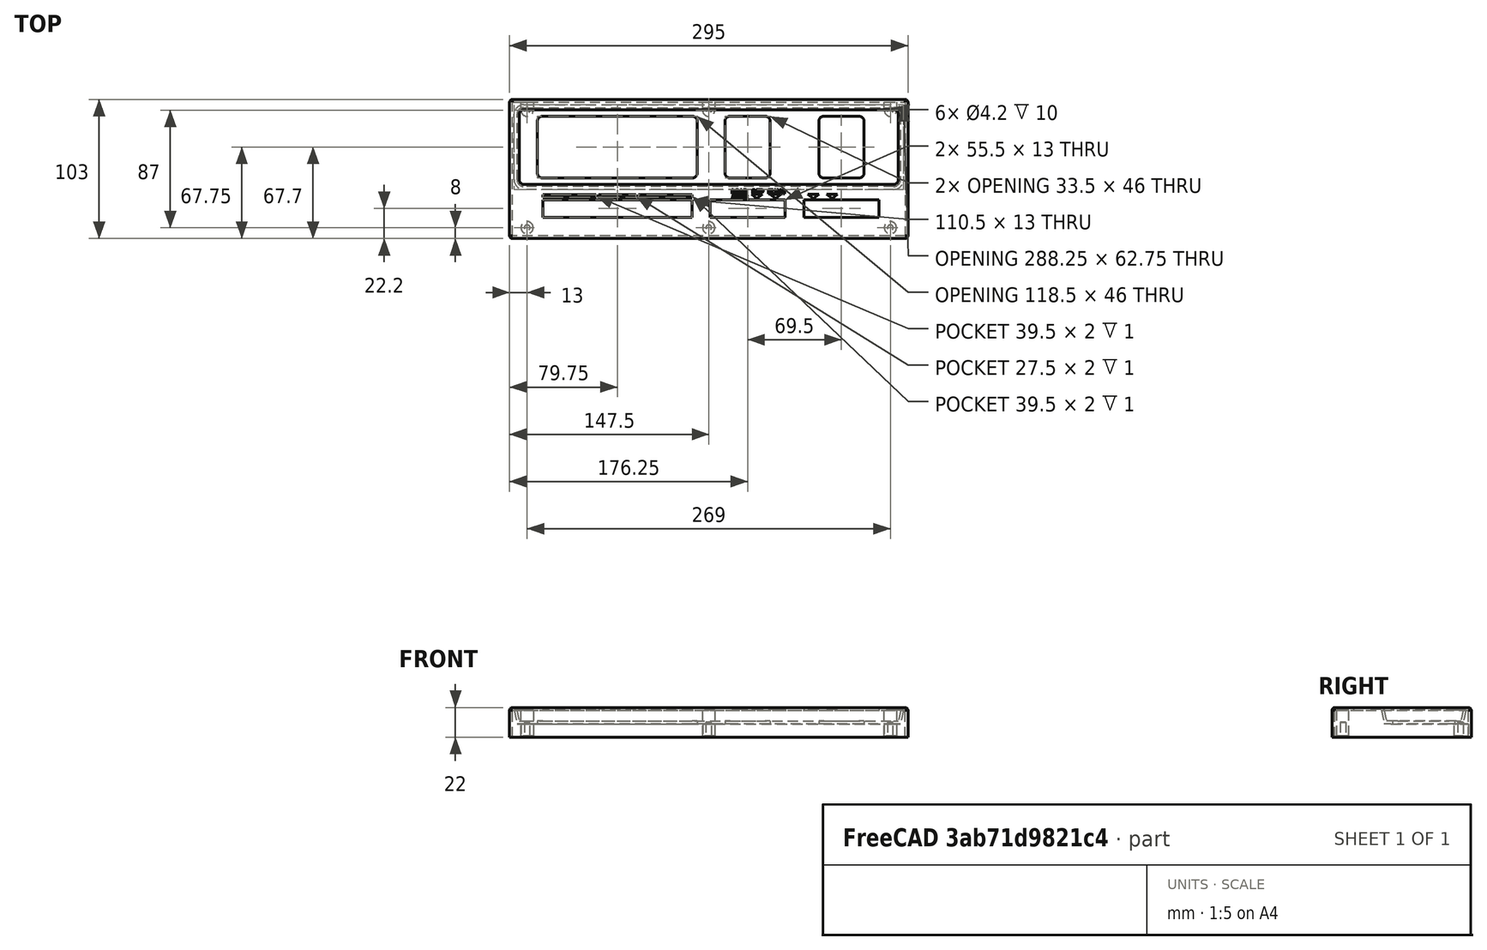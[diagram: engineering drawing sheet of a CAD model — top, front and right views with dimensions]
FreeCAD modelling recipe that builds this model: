
FCSTD DOCUMENT  (FreeCAD 0.21R33771 (Git))
Label: front panel
License: All rights reserved
LicenseURL: http://en.wikipedia.org/wiki/All_rights_reserved
objects: PartDesign::Pocket×8, Sketcher::SketchObject×7, PartDesign::LinearPattern×4, Part::Part2DObjectPython×4, PartDesign::Pad×3, TechDraw::DrawViewDimension×3, PartDesign::Draft×1, PartDesign::Thickness×1, PartDesign::MultiTransform×1, TechDraw::DrawSVGTemplate×1, PartDesign::Body×1, TechDraw::DrawProjGroupItem×1, TechDraw::DrawProjGroup×1, TechDraw::DrawPage×1
note: 48 computed .brp shape members not serialized (recipe doc carries the construction recipe); baked Part::Feature solids carry a one-line shape summary decoded from their .brp

FEATURE [Sketcher::SketchObject] Sketch
  FullyConstrained = true
  MapMode = 5
  Support = -> [XY_Plane]
  sketch-geometry (4):
    g0: LineSegment StartX=-145.5 StartY=49.5 StartZ=0 EndX=145.5 EndY=49.5 EndZ=0
    g1: LineSegment StartX=145.5 StartY=49.5 StartZ=0 EndX=145.5 EndY=-49.5 EndZ=0
    g2: LineSegment StartX=145.5 StartY=-49.5 StartZ=0 EndX=-145.5 EndY=-49.5 EndZ=0
    g3: LineSegment StartX=-145.5 StartY=-49.5 StartZ=0 EndX=-145.5 EndY=49.5 EndZ=0
  constraints (11):
    c: Coincident(g0,g1)
    c: Coincident(g1,g2)
    c: Coincident(g2,g3)
    c: Coincident(g3,g0)
    c: Horizontal(g0)
    c: Horizontal(g2)
    c: Vertical(g1)
    c: Vertical(g3)
    c: Symmetric(g1,g0,g-1)
    c: DistanceY(g3,g3) = 99
    c: DistanceX(g0,g0) = 291
FEATURE [PartDesign::Pad] Pad
  Direction = (0,0,1)
  Length = 20
  Length2 = 10
  Profile = -> Sketch
  ReferenceAxis = -> Sketch [N_Axis]
  Type = 0
FEATURE [Sketcher::SketchObject] Sketch001
  FullyConstrained = true
  MapMode = 5
  Placement = pos=(0,0,20) rot=(0,0,1;0rad)
  Support = -> [Pad]
  sketch-geometry (10):
    g0: ArcOfCircle CenterX=-137 CenterY=40.5 CenterZ=0 NormalX=0 NormalY=0 NormalZ=1 AngleXU=0 Radius=5 StartAngle=1.5708 EndAngle=3.14159
    g1: LineSegment StartX=-137 StartY=45.5 StartZ=0 EndX=137 EndY=45.5 EndZ=0
    g2: ArcOfCircle CenterX=137 CenterY=40.5 CenterZ=0 NormalX=0 NormalY=0 NormalZ=1 AngleXU=0 Radius=5 StartAngle=5e-16 EndAngle=1.5708
    g3: LineSegment StartX=142 StartY=40.5 StartZ=0 EndX=142 EndY=-8 EndZ=0
    g4: ArcOfCircle CenterX=137 CenterY=-8 CenterZ=0 NormalX=0 NormalY=0 NormalZ=1 AngleXU=0 Radius=5 StartAngle=4.71239 EndAngle=6.28319
    g5: LineSegment StartX=137 StartY=-13 StartZ=0 EndX=-137 EndY=-13 EndZ=0
    g6: ArcOfCircle CenterX=-137 CenterY=-8 CenterZ=0 NormalX=0 NormalY=0 NormalZ=1 AngleXU=0 Radius=5 StartAngle=3.14159 EndAngle=4.71239
    g7: LineSegment StartX=-142 StartY=-8 StartZ=0 EndX=-142 EndY=40.5 EndZ=0
    g8: GeomPoint X=-142 Y=45.5 Z=0
    g9: GeomPoint X=142 Y=-13 Z=0
  constraints (23):
    c: Tangent(g0,g1) = 1.5708
    c: Tangent(g1,g2) = 1.5708
    c: Tangent(g2,g3) = 1.5708
    c: Tangent(g3,g4) = 1.5708
    c: Tangent(g4,g5) = 1.5708
    c: Tangent(g5,g6) = 1.5708
    c: Tangent(g6,g7) = 1.5708
    c: Tangent(g7,g0) = 1.5708
    c: Horizontal(g1)
    c: Horizontal(g5)
    c: Vertical(g3)
    c: Vertical(g7)
    c: Equal(g2,g4)
    c: Equal(g4,g6)
    c: PointOnObject(g8,g1)
    c: PointOnObject(g8,g7)
    c: PointOnObject(g9,g3)
    c: PointOnObject(g9,g5)
    c: Diameter(g2) = 10
    c: DistanceX(g0,g2) = 284
    c: Symmetric(g0,g2,g-2)
    c: DistanceY(g-1,g0) = 45.5
    c: DistanceY(g5,g-1) = 13
FEATURE [PartDesign::Pocket] Pocket
  BaseFeature = -> Pad
  Direction = (0,0,-1)
  Length = 10
  Length2 = 5
  Profile = -> Sketch001
  ReferenceAxis = -> Sketch001 [N_Axis]
  Type = 0
FEATURE [PartDesign::Draft] Draft
  Angle = 12
  Base = -> Pocket [Face10]
  BaseFeature = -> Pocket
  NeutralPlane = -> Pocket [Face15]
  SupportTransform = false
FEATURE [PartDesign::Thickness] Thickness
  Base = -> Draft [Face4]
  BaseFeature = -> Draft
  Intersection = false
  Join = 0
  Mode = 0
  SupportTransform = false
  Value = 2
FEATURE [Sketcher::SketchObject] Sketch002
  FullyConstrained = true
  MapMode = 5
  Placement = pos=(0,0,22) rot=(0,0,1;0rad)
  Support = -> [Thickness]
  sketch-geometry (42):
    g0: LineSegment StartX=-123 StartY=-22.8 StartZ=0 EndX=-12.5 EndY=-22.8 EndZ=0
    g1: LineSegment StartX=-12.5 StartY=-22.8 StartZ=0 EndX=-12.5 EndY=-35.8 EndZ=0
    g2: LineSegment StartX=-12.5 StartY=-35.8 StartZ=0 EndX=-123 EndY=-35.8 EndZ=0
    g3: LineSegment StartX=-123 StartY=-35.8 StartZ=0 EndX=-123 EndY=-22.8 EndZ=0
    g4: LineSegment StartX=1 StartY=-22.8 StartZ=0 EndX=56.5 EndY=-22.8 EndZ=0
    g5: LineSegment StartX=56.5 StartY=-22.8 StartZ=0 EndX=56.5 EndY=-35.8 EndZ=0
    g6: LineSegment StartX=56.5 StartY=-35.8 StartZ=0 EndX=1 EndY=-35.8 EndZ=0
    g7: LineSegment StartX=1 StartY=-35.8 StartZ=0 EndX=1 EndY=-22.8 EndZ=0
    g8: LineSegment StartX=70.5 StartY=-22.8 StartZ=0 EndX=126 EndY=-22.8 EndZ=0
    g9: LineSegment StartX=126 StartY=-22.8 StartZ=0 EndX=126 EndY=-35.8 EndZ=0
    g10: LineSegment StartX=126 StartY=-35.8 StartZ=0 EndX=70.5 EndY=-35.8 EndZ=0
    g11: LineSegment StartX=70.5 StartY=-35.8 StartZ=0 EndX=70.5 EndY=-22.8 EndZ=0
    g12: ArcOfCircle CenterX=-123 CenterY=35.2 CenterZ=0 NormalX=0 NormalY=0 NormalZ=1 AngleXU=0 Radius=4 StartAngle=1.5708 EndAngle=3.14159
    g13: LineSegment StartX=-123 StartY=39.2 StartZ=0 EndX=-12.5 EndY=39.2 EndZ=0
    g14: ArcOfCircle CenterX=-12.5 CenterY=35.2 CenterZ=0 NormalX=0 NormalY=0 NormalZ=1 AngleXU=0 Radius=4 StartAngle=7e-16 EndAngle=1.5708
    g15: LineSegment StartX=-8.5 StartY=35.2 StartZ=0 EndX=-8.5 EndY=-2.8 EndZ=0
    g16: ArcOfCircle CenterX=-12.5 CenterY=-2.8 CenterZ=0 NormalX=0 NormalY=0 NormalZ=1 AngleXU=0 Radius=4 StartAngle=4.71239 EndAngle=6.28319
    g17: LineSegment StartX=-12.5 StartY=-6.8 StartZ=0 EndX=-123 EndY=-6.8 EndZ=0
    g18: ArcOfCircle CenterX=-123 CenterY=-2.8 CenterZ=0 NormalX=0 NormalY=0 NormalZ=1 AngleXU=0 Radius=4 StartAngle=3.14159 EndAngle=4.71239
    g19: LineSegment StartX=-127 StartY=-2.8 StartZ=0 EndX=-127 EndY=35.2 EndZ=0
    g20: GeomPoint X=-127 Y=39.2 Z=0
    g21: GeomPoint X=-8.5 Y=-6.8 Z=0
    g22: ArcOfCircle CenterX=16 CenterY=35.2 CenterZ=0 NormalX=0 NormalY=0 NormalZ=1 AngleXU=0 Radius=4 StartAngle=1.5708 EndAngle=3.14159
    g23: LineSegment StartX=16 StartY=39.2 StartZ=0 EndX=41.5 EndY=39.2 EndZ=0
    g24: ArcOfCircle CenterX=41.5 CenterY=35.2 CenterZ=0 NormalX=0 NormalY=0 NormalZ=1 AngleXU=0 Radius=4 StartAngle=1e-15 EndAngle=1.5708
    g25: LineSegment StartX=45.5 StartY=35.2 StartZ=0 EndX=45.5 EndY=-2.8 EndZ=0
    g26: ArcOfCircle CenterX=41.5 CenterY=-2.8 CenterZ=0 NormalX=0 NormalY=0 NormalZ=1 AngleXU=0 Radius=4 StartAngle=4.71239 EndAngle=6.28319
    g27: LineSegment StartX=41.5 StartY=-6.8 StartZ=0 EndX=16 EndY=-6.8 EndZ=0
    g28: ArcOfCircle CenterX=16 CenterY=-2.8 CenterZ=0 NormalX=0 NormalY=0 NormalZ=1 AngleXU=0 Radius=4 StartAngle=3.14159 EndAngle=4.71239
    g29: LineSegment StartX=12 StartY=-2.8 StartZ=0 EndX=12 EndY=35.2 EndZ=0
    g30: GeomPoint X=12 Y=39.2 Z=0
    g31: GeomPoint X=45.5 Y=-6.8 Z=0
    g32: ArcOfCircle CenterX=85.5 CenterY=35.2 CenterZ=0 NormalX=0 NormalY=0 NormalZ=1 AngleXU=0 Radius=4 StartAngle=1.5708 EndAngle=3.14159
    g33: LineSegment StartX=85.5 StartY=39.2 StartZ=0 EndX=111 EndY=39.2 EndZ=0
    g34: ArcOfCircle CenterX=111 CenterY=35.2 CenterZ=0 NormalX=0 NormalY=0 NormalZ=1 AngleXU=0 Radius=4 StartAngle=1e-15 EndAngle=1.5708
    g35: LineSegment StartX=115 StartY=35.2 StartZ=0 EndX=115 EndY=-2.8 EndZ=0
    g36: ArcOfCircle CenterX=111 CenterY=-2.8 CenterZ=0 NormalX=0 NormalY=0 NormalZ=1 AngleXU=0 Radius=4 StartAngle=4.71239 EndAngle=6.28319
    g37: LineSegment StartX=111 StartY=-6.8 StartZ=0 EndX=85.5 EndY=-6.8 EndZ=0
    g38: ArcOfCircle CenterX=85.5 CenterY=-2.8 CenterZ=0 NormalX=0 NormalY=0 NormalZ=1 AngleXU=0 Radius=4 StartAngle=3.14159 EndAngle=4.71239
    g39: LineSegment StartX=81.5 StartY=-2.8 StartZ=0 EndX=81.5 EndY=35.2 EndZ=0
    g40: GeomPoint X=81.5 Y=39.2 Z=0
    g41: GeomPoint X=115 Y=-6.8 Z=0
  constraints (108):
    c: Coincident(g0,g1)
    c: Coincident(g1,g2)
    c: Coincident(g2,g3)
    c: Coincident(g3,g0)
    c: Horizontal(g0)
    c: Horizontal(g2)
    c: Vertical(g1)
    c: Vertical(g3)
    c: Coincident(g4,g5)
    c: Coincident(g5,g6)
    c: Coincident(g6,g7)
    c: Coincident(g7,g4)
    c: Horizontal(g4)
    c: Horizontal(g6)
    c: Vertical(g5)
    c: Vertical(g7)
    c: Coincident(g8,g9)
    c: Coincident(g9,g10)
    c: Coincident(g10,g11)
    c: Coincident(g11,g8)
    c: Horizontal(g8)
    c: Horizontal(g10)
    c: Vertical(g9)
    c: Vertical(g11)
    c: Horizontal(g10,g5)
    c: Horizontal(g5,g1)
    c: Horizontal(g4,g0)
    c: Horizontal(g0,g8)
    c: DistanceY(g3,g3) = 13
    c: DistanceX(g2,g-1) = 123
    c: DistanceX(g0,g0) = 110.5
    c: DistanceY(g1,g-1) = 35.8
    c: DistanceX(g0,g4) = 13.5
    c: DistanceX(g4,g4) = 55.5
    c: DistanceX(g4,g8) = 14
    c: Equal(g8,g4)
    c: Tangent(g12,g13) = 1.5708
    c: Tangent(g13,g14) = 1.5708
    c: Tangent(g14,g15) = 1.5708
    c: Tangent(g15,g16) = 1.5708
    c: Tangent(g16,g17) = 1.5708
    c: Tangent(g17,g18) = 1.5708
    c: Tangent(g18,g19) = 1.5708
    c: Tangent(g19,g12) = 1.5708
    c: Horizontal(g13)
    c: Horizontal(g17)
    c: Vertical(g15)
    c: Vertical(g19)
    c: Equal(g12,g14)
    c: Equal(g14,g16)
    c: Equal(g16,g18)
    c: PointOnObject(g20,g13)
    c: PointOnObject(g20,g19)
    c: PointOnObject(g21,g15)
    c: PointOnObject(g21,g17)
    c: Radius(g12) = 4
    c: Vertical(g17,g0)
    c: Vertical(g16,g0)
    c: Tangent(g22,g23) = 1.5708
    c: Tangent(g23,g24) = 1.5708
    c: Tangent(g24,g25) = 1.5708
    c: Tangent(g25,g26) = 1.5708
    c: Tangent(g26,g27) = 1.5708
    c: Tangent(g27,g28) = 1.5708
    c: Tangent(g28,g29) = 1.5708
    c: Tangent(g29,g22) = 1.5708
    c: Horizontal(g23)
    c: Horizontal(g27)
    c: Vertical(g25)
    c: Vertical(g29)
    c: Equal(g22,g24)
    c: Equal(g24,g26)
    c: Equal(g26,g28)
    c: PointOnObject(g30,g23)
    c: PointOnObject(g30,g29)
    c: PointOnObject(g31,g25)
    c: PointOnObject(g31,g27)
    c: Equal(g26,g14)
    c: Horizontal(g22,g13)
    c: Horizontal(g27,g16)
    c: DistanceX(g26,g4) = 15
    c: DistanceX(g4,g27) = 15
    c: Tangent(g32,g33) = 1.5708
    c: Tangent(g33,g34) = 1.5708
    c: Tangent(g34,g35) = 1.5708
    c: Tangent(g35,g36) = 1.5708
    c: Tangent(g36,g37) = 1.5708
    c: Tangent(g37,g38) = 1.5708
    c: Tangent(g38,g39) = 1.5708
    c: Tangent(g39,g32) = 1.5708
    c: Horizontal(g33)
    c: Horizontal(g37)
    c: Vertical(g35)
    c: Vertical(g39)
    c: Equal(g32,g34)
    c: Equal(g34,g36)
    c: Equal(g36,g38)
    c: PointOnObject(g40,g33)
    c: PointOnObject(g40,g39)
    c: PointOnObject(g41,g35)
    c: PointOnObject(g41,g37)
    c: Horizontal(g23,g32)
    c: Equal(g32,g24)
    c: DistanceX(g36,g8) = 15
    c: Equal(g27,g37)
    c: DistanceY(g8,g35) = 20
    c: DistanceY(g8,g33) = 62
    c: Horizontal(g37,g16)
FEATURE [PartDesign::Pocket] Pocket001  label="Switch cut out"
  BaseFeature = -> Thickness
  Direction = (0,0,-1)
  Length = 5
  Length2 = 5
  Profile = -> Sketch002
  ReferenceAxis = -> Sketch002 [N_Axis]
  Type = 1
FEATURE [Sketcher::SketchObject] Sketch003
  FullyConstrained = true
  MapMode = 5
  Placement = pos=(0,0,20) rot=(1,0,0;3.14159rad)
  Support = -> [Pocket001]
  sketch-geometry (1):
    g0: Circle CenterX=-134.5 CenterY=43.5 CenterZ=0 NormalX=0 NormalY=0 NormalZ=1 AngleXU=0 Radius=4.5
  constraints (3):
    c: DistanceY(g-1,g0) = 43.5
    c: DistanceX(g0,g-1) = 134.5
    c: Diameter(g0) = 9
FEATURE [PartDesign::Pad] Pad001
  BaseFeature = -> Pocket001
  Direction = (0,0,-1)
  Length = 19
  Length2 = 10
  Profile = -> Sketch003
  ReferenceAxis = -> Sketch003 [N_Axis]
  Type = 0
FEATURE [PartDesign::LinearPattern] LinearPattern
  BaseFeature = -> Pad001
  Direction = -> Sketch003 [H_Axis]
  Length = 269
  Occurrences = 3
  Originals = -> [Pad001]
FEATURE [Sketcher::SketchObject] Sketch004
  ExternalGeometry = -> [LinearPattern]
  FullyConstrained = true
  MapMode = 5
  Placement = pos=(0,0,10) rot=(1,0,0;3.14159rad)
  Support = -> [LinearPattern]
  sketch-geometry (4):
    g0: ArcOfCircle CenterX=-134.5 CenterY=-43.5 CenterZ=0 NormalX=0 NormalY=0 NormalZ=1 AngleXU=0 Radius=4.5 StartAngle=-9e-16 EndAngle=3.14159
    g1: LineSegment StartX=-139 StartY=-43.5 StartZ=0 EndX=-139 EndY=-49.5 EndZ=0
    g2: LineSegment StartX=-139 StartY=-49.5 StartZ=0 EndX=-130 EndY=-49.5 EndZ=0
    g3: LineSegment StartX=-130 StartY=-49.5 StartZ=0 EndX=-130 EndY=-43.5 EndZ=0
  constraints (11):
    c: Tangent(g0,g1) = -1.5708
    c: Coincident(g1,g2)
    c: PointOnObject(g2,g-3)
    c: Horizontal(g2)
    c: Coincident(g2,g3)
    c: Vertical(g3)
    c: Vertical(g1)
    c: Diameter(g0) = 9
    c: DistanceX(g0,g-1) = 134.5
    c: DistanceY(g0,g-1) = 43.5
    c: Tangent(g3,g0) = -1.5708
FEATURE [PartDesign::Pad] Pad002
  BaseFeature = -> LinearPattern
  Direction = (0,0,-1)
  Length = 9
  Length2 = 10
  Profile = -> Sketch004
  ReferenceAxis = -> Sketch004 [N_Axis]
  Type = 0
FEATURE [PartDesign::LinearPattern] LinearPattern001
  BaseFeature = -> Pad002
  Direction = -> Sketch004 [H_Axis]
  Length = 269
  Occurrences = 3
  Originals = -> [Pad002]
FEATURE [Sketcher::SketchObject] Sketch005
  ExternalGeometry = -> [LinearPattern001]
  FullyConstrained = true
  MapMode = 5
  Placement = pos=(0,0,1) rot=(1,0,0;3.14159rad)
  Support = -> [LinearPattern001]
  sketch-geometry (1):
    g0: Circle CenterX=-134.5 CenterY=43.5 CenterZ=0 NormalX=0 NormalY=0 NormalZ=1 AngleXU=0 Radius=2.1
  constraints (2):
    c: Coincident(g0,g-3)
    c: Diameter(g0) = 4.2
FEATURE [PartDesign::Pocket] Pocket002
  BaseFeature = -> LinearPattern001
  Direction = (0,0,1)
  Length = 10
  Length2 = 5
  Profile = -> Sketch005
  ReferenceAxis = -> Sketch005 [N_Axis]
  Type = 0
FEATURE [PartDesign::LinearPattern] LinearPattern002
  Direction = -> Sketch005 [H_Axis]
  Length = 269
  Occurrences = 3
FEATURE [PartDesign::LinearPattern] LinearPattern003
  Direction = -> Sketch005 [V_Axis]
  Length = 87
  Occurrences = 2
  Reversed = true
FEATURE [PartDesign::MultiTransform] MultiTransform
  BaseFeature = -> Pocket002
  Originals = -> [Pocket002]
  Transformations = -> [LinearPattern002,LinearPattern003]
FEATURE [TechDraw::DrawSVGTemplate] Template
  EditableTexts = APPROVER_NAME=APPROVER NAME; AUTHOR_NAME=AUTHOR NAME; DATE=YYYY-MM-DD; DN=DN; DOCUMENT_TYPE=Mechanical assembly drawing; OWNER_NAME=OWNER NAME; PM=PM; PN=PN; REVISION=REV A; RIGHTS=(R) DO NOT DUPLICATE THIS DRAWING TO THIRD PARTIES WITHOUT OWNER'S PERMISSION!; SCALE=M x:x; SHEET=99 of 99; SIZE=A3; TITLELINE-1=FreeCAD; TOLERANCE=+/- ?
  Height = 297
  Orientation = 1
  Template = /Applications/FreeCAD.app/Contents/Resources/share/Mod/TechDraw/Templates/A3_Landscape_ISO7200_Pep.svg
  Width = 420
FEATURE [Sketcher::SketchObject] Sketch006
  ExternalGeometry = -> [MultiTransform]
  FullyConstrained = true
  MapMode = 5
  Placement = pos=(0,0,22) rot=(0,0,1;0rad)
  Support = -> [MultiTransform]
  sketch-geometry (28):
    g0: LineSegment StartX=-123 StartY=-19.098 StartZ=0 EndX=-83.5 EndY=-19.098 EndZ=0
    g1: LineSegment StartX=-83.5 StartY=-19.098 StartZ=0 EndX=-83.5 EndY=-21.098 EndZ=0
    g2: LineSegment StartX=-83.5 StartY=-21.098 StartZ=0 EndX=-123 EndY=-21.098 EndZ=0
    g3: LineSegment StartX=-123 StartY=-21.098 StartZ=0 EndX=-123 EndY=-19.098 EndZ=0
    g4: LineSegment StartX=-81.5 StartY=-19.098 StartZ=0 EndX=-54 EndY=-19.098 EndZ=0
    g5: LineSegment StartX=-54 StartY=-19.098 StartZ=0 EndX=-54 EndY=-21.098 EndZ=0
    g6: LineSegment StartX=-54 StartY=-21.098 StartZ=0 EndX=-81.5 EndY=-21.098 EndZ=0
    g7: LineSegment StartX=-81.5 StartY=-21.098 StartZ=0 EndX=-81.5 EndY=-19.098 EndZ=0
    g8: LineSegment StartX=-52 StartY=-19.098 StartZ=0 EndX=-12.5 EndY=-19.098 EndZ=0
    g9: LineSegment StartX=-12.5 StartY=-19.098 StartZ=0 EndX=-12.5 EndY=-21.098 EndZ=0
    g10: LineSegment StartX=-12.5 StartY=-21.098 StartZ=0 EndX=-52 EndY=-21.098 EndZ=0
    g11: LineSegment StartX=-52 StartY=-21.098 StartZ=0 EndX=-52 EndY=-19.098 EndZ=0
    g12: LineSegment StartX=53.5 StartY=-18.8 StartZ=0 EndX=45.5 EndY=-18.8 EndZ=0
    g13: LineSegment StartX=45.5 StartY=-18.8 StartZ=0 EndX=49.5 EndY=-21.8 EndZ=0
    g14: LineSegment StartX=49.5 StartY=-21.8 StartZ=0 EndX=53.5 EndY=-18.8 EndZ=0
    g15: Circle CenterX=49.5 CenterY=-17.6333 CenterZ=0 NormalX=0 NormalY=0 NormalZ=1 AngleXU=0 Radius=4.16667
    g16: LineSegment StartX=35.7 StartY=-21.8 StartZ=0 EndX=39.7 EndY=-18.8 EndZ=0
    g17: LineSegment StartX=39.7 StartY=-18.8 StartZ=0 EndX=31.7 EndY=-18.8 EndZ=0
    g18: LineSegment StartX=31.7 StartY=-18.8 StartZ=0 EndX=35.7 EndY=-21.8 EndZ=0
    g19: Circle CenterX=35.7 CenterY=-17.6333 CenterZ=0 NormalX=0 NormalY=0 NormalZ=1 AngleXU=0 Radius=4.16667
    g20: LineSegment StartX=77.5 StartY=-21.8 StartZ=0 EndX=81.5 EndY=-18.8 EndZ=0
    g21: LineSegment StartX=81.5 StartY=-18.8 StartZ=0 EndX=73.5 EndY=-18.8 EndZ=0
    g22: LineSegment StartX=73.5 StartY=-18.8 StartZ=0 EndX=77.5 EndY=-21.8 EndZ=0
    g23: Circle CenterX=77.5 CenterY=-17.6333 CenterZ=0 NormalX=0 NormalY=0 NormalZ=1 AngleXU=0 Radius=4.16667
    g24: LineSegment StartX=91.3 StartY=-21.8 StartZ=0 EndX=95.3 EndY=-18.8 EndZ=0
    g25: LineSegment StartX=95.3 StartY=-18.8 StartZ=0 EndX=87.3 EndY=-18.8 EndZ=0
    g26: LineSegment StartX=87.3 StartY=-18.8 StartZ=0 EndX=91.3 EndY=-21.8 EndZ=0
    g27: Circle CenterX=91.3 CenterY=-17.6333 CenterZ=0 NormalX=0 NormalY=0 NormalZ=1 AngleXU=0 Radius=4.16667
  constraints (84):
    c: Coincident(g0,g1)
    c: Coincident(g1,g2)
    c: Coincident(g2,g3)
    c: Coincident(g3,g0)
    c: Horizontal(g0)
    c: Horizontal(g2)
    c: Vertical(g1)
    c: Vertical(g3)
    c: Coincident(g4,g5)
    c: Coincident(g5,g6)
    c: Coincident(g6,g7)
    c: Coincident(g7,g4)
    c: Horizontal(g4)
    c: Horizontal(g6)
    c: Vertical(g5)
    c: Vertical(g7)
    c: Coincident(g8,g9)
    c: Coincident(g9,g10)
    c: Coincident(g10,g11)
    c: Coincident(g11,g8)
    c: Horizontal(g8)
    c: Horizontal(g10)
    c: Vertical(g9)
    c: Vertical(g11)
    c: DistanceY(g3,g3) = 2
    c: Vertical(g2,g-3)
    c: Equal(g8,g0)
    c: Horizontal(g6,g1)
    c: Horizontal(g1,g10)
    c: Horizontal(g8,g4)
    c: Horizontal(g4,g0)
    c: Vertical(g9,g-4)
    c: DistanceY(g-3,g2) = 1.702
    c: DistanceX(g0,g4) = 2
    c: DistanceX(g4,g8) = 2
    c: DistanceX(g8,g8) = 39.5
    c: Coincident(g12,g13)
    c: Coincident(g13,g14)
    c: Coincident(g14,g12)
    c: PointOnObject(g12,g15)
    c: PointOnObject(g13,g15)
    c: PointOnObject(g14,g15)
    c: Coincident(g16,g17)
    c: Coincident(g17,g18)
    c: Coincident(g18,g16)
    c: Equal(g16,g18)
    c: PointOnObject(g16,g19)
    c: PointOnObject(g17,g19)
    c: PointOnObject(g18,g19)
    c: Horizontal(g17)
    c: Horizontal(g12)
    c: Equal(g16,g13)
    c: DistanceX(g19,g15) = 13.8
    c: Equal(g17,g12)
    c: Horizontal(g16,g12)
    c: Equal(g14,g13)
    c: DistanceX(g17,g17) = 8
    c: DistanceY(g16,g16) = 3
    c: DistanceX(g13,g-5) = 7
    c: DistanceY(g-5,g13) = 1
    c: Coincident(g20,g21)
    c: Coincident(g21,g22)
    c: Coincident(g22,g20)
    c: Equal(g20,g22)
    c: PointOnObject(g20,g23)
    c: PointOnObject(g21,g23)
    c: PointOnObject(g22,g23)
    c: Coincident(g24,g25)
    c: Coincident(g25,g26)
    c: Coincident(g26,g24)
    c: Equal(g24,g26)
    c: PointOnObject(g24,g27)
    c: PointOnObject(g25,g27)
    c: PointOnObject(g26,g27)
    c: Horizontal(g25,g20)
    c: Horizontal(g25)
    c: Horizontal(g21)
    c: DistanceX(g23,g27) = 13.8
    c: Equal(g21,g25)
    c: Equal(g25,g12)
    c: DistanceY(g20,g20) = 3
    c: Horizontal(g24,g20)
    c: Horizontal(g12,g21)
    c: DistanceX(g-6,g20) = 7
FEATURE [PartDesign::Pocket] Pocket003  label="Down arrows"
  BaseFeature = -> MultiTransform
  Direction = (0,0,-1)
  Length = 1
  Length2 = 5
  Profile = -> Sketch006
  ReferenceAxis = -> Sketch006 [N_Axis]
  Type = 0
FEATURE [Part::Part2DObjectPython] ShapeString  label="DEP"  # Draft 2D object (typed FeaturePython)
  FontFile = <userpath>/Downloads/roboto/Roboto-Black.ttf
  MakeFace = true
  Placement = pos=(32,-18.5,22) rot=(0,0,1;0rad)
  Size = 4
  String = DEP
  Tracking = 0
FEATURE [Part::Part2DObjectPython] ShapeString001  label="LOAD"  # Draft 2D object (typed FeaturePython)
  FontFile = <userpath>/Downloads/roboto/Roboto-Black.ttf
  MakeFace = true
  Placement = pos=(17,-18.5,22) rot=(0,0,1;0rad)
  Size = 4
  String = LOAD
  Tracking = 0
FEATURE [Part::Part2DObjectPython] ShapeString002  label="ADDR"  # Draft 2D object (typed FeaturePython)
  FontFile = <userpath>/Downloads/roboto/Roboto-Black.ttf
  MakeFace = true
  Placement = pos=(17,-22.25,22) rot=(0.987988,-0.125405,-0.090301;0rad)
  Size = 4
  String = ADDR
  Tracking = 0
FEATURE [PartDesign::Pocket] Pocket004  label="DEP Pocket"
  BaseFeature = -> Pocket003
  Direction = (0,0,-1)
  Length = 1
  Length2 = 5
  Profile = -> ShapeString
  ReferenceAxis = -> ShapeString [N_Axis]
  Type = 0
FEATURE [PartDesign::Pocket] Pocket005  label="Load Pocket"
  BaseFeature = -> Pocket004
  Direction = (0,0,-1)
  Length = 1
  Length2 = 5
  Profile = -> ShapeString001
  ReferenceAxis = -> ShapeString001 [N_Axis]
  Type = 0
FEATURE [PartDesign::Pocket] Pocket006  label="ADDR Pocket"
  BaseFeature = -> Pocket005
  Direction = (0,0,-1)
  Length = 1
  Length2 = 5
  Profile = -> ShapeString002
  ReferenceAxis = -> ShapeString002 [N_Axis]
  Type = 0
FEATURE [Part::Part2DObjectPython] ShapeString003  label="EXAM"  # Draft 2D object (typed FeaturePython)
  FontFile = <userpath>/Downloads/roboto/Roboto-Black.ttf
  MakeFace = true
  Placement = pos=(44,-18.5,22) rot=(0,0,1;0rad)
  Size = 4
  String = EXAM
  Tracking = 0
FEATURE [PartDesign::Pocket] Pocket007
  BaseFeature = -> Pocket006
  Direction = (0,0,-1)
  Length = 1
  Length2 = 5
  Profile = -> ShapeString003
  ReferenceAxis = -> ShapeString003 [N_Axis]
  Type = 0
FEATURE [PartDesign::Body] Body
  Group = -> [Sketch,Pad,Sketch001,Pocket,Draft,Thickness,Sketch002,Pocket001,Sketch003,Pad001,LinearPattern,Sketch004,Pad002,LinearPattern001,Sketch005,Pocket002,MultiTransform,LinearPattern002,LinearPattern003,Sketch006,Pocket003,ShapeString,ShapeString001,ShapeString002,Pocket004,Pocket005,Pocket006,ShapeString003,Pocket007]
  Origin = -> Origin
  Tip = -> Pocket007
FEATURE [TechDraw::DrawProjGroupItem] ProjItem  label="Front"
  CoarseView = false
  Direction = (0,0,1)
  Focus = 100
  HardHidden = false
  IsoCount = 0
  IsoHidden = false
  IsoVisible = false
  LockPosition = true
  Perspective = false
  Rotation = 0
  RotationVector = (1,0,0)
  ScaleType = 2
  ScrubCount = 0
  SeamHidden = false
  SeamVisible = true
  SmoothHidden = false
  SmoothVisible = true
  Source = -> [Body]
  Type = 0
  X = 0
  XDirection = (1,0,0)
  Y = 0
FEATURE [TechDraw::DrawProjGroup] ProjGroup
  Anchor = -> ProjItem
  AutoDistribute = true
  LockPosition = false
  ProjectionType = 0
  Rotation = 0
  ScaleType = 0
  Source = -> [Body]
  Views = -> [ProjItem]
  X = 210
  Y = 148.5
  spacingX = 15
  spacingY = 15
FEATURE [TechDraw::DrawViewDimension] Dimension001
  AngleOverride = false
  Arbitrary = false
  ArbitraryTolerances = false
  EqualTolerance = true
  ExtensionAngle = 0
  FormatSpec = %.3f
  FormatSpecOverTolerance = %+.3f
  FormatSpecUnderTolerance = %+.3f
  Inverted = false
  LineAngle = 0
  LockPosition = false
  MeasureType = 1
  OverTolerance = 0
  References2D = -> [ProjItem]
  Rotation = 0
  ScaleType = 0
  TheoreticalExact = false
  Type = 2
  UnderTolerance = 0
  X = 168.608
  Y = 20.4136
FEATURE [TechDraw::DrawViewDimension] Dimension002
  AngleOverride = false
  Arbitrary = false
  ArbitraryTolerances = false
  EqualTolerance = true
  ExtensionAngle = 0
  FormatSpec = R%.3f
  FormatSpecOverTolerance = %+.3f
  FormatSpecUnderTolerance = %+.3f
  Inverted = false
  LineAngle = 0
  LockPosition = false
  MeasureType = 1
  OverTolerance = 0
  References2D = -> [ProjItem]
  Rotation = 0
  ScaleType = 0
  TheoreticalExact = false
  Type = 4
  UnderTolerance = 0
  X = -162.459
  Y = 43.8237
FEATURE [TechDraw::DrawViewDimension] Dimension
  AngleOverride = false
  Arbitrary = false
  ArbitraryTolerances = false
  EqualTolerance = true
  ExtensionAngle = 0
  FormatSpec = %.3f
  FormatSpecOverTolerance = %+.3f
  FormatSpecUnderTolerance = %+.3f
  Inverted = false
  LineAngle = 0
  LockPosition = false
  MeasureType = 1
  OverTolerance = 0
  References2D = -> [ProjItem]
  Rotation = 0
  ScaleType = 0
  TheoreticalExact = false
  Type = 1
  UnderTolerance = 0
  X = -6.9642
  Y = 88.1732
FEATURE [TechDraw::DrawPage] Page
  KeepUpdated = true
  NextBalloonIndex = 1
  ProjectionType = 0
  Template = -> Template
  Views = -> [ProjGroup,Dimension001,Dimension002,Dimension]
